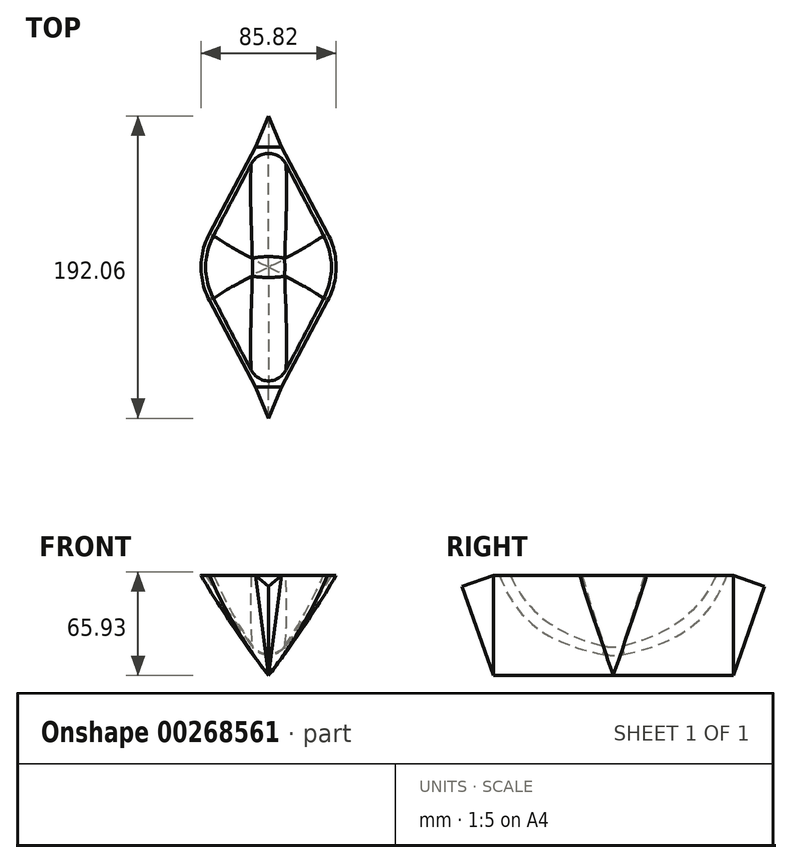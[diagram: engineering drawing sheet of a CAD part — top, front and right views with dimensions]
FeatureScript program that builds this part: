
annotation { "Feature Type Name" : "Feature", "Feature Type Description" : "" }
export const myFeature = defineFeature(function(context is Context, id is Id, definition is map)
    precondition{}
    {
        {
            var Q0;
            Q0=qCreatedBy(makeId("Front.planeOp"),FACE);
            var sketch = newSketch(context, id + "F0", { "sketchPlane" : qUnion([Q0])});
            skLineSegment(sketch, "E0", {"start": v(0, 0) * mm, "end": v(-48.84, 63.76) * mm});
            skLineSegment(sketch, "E1", {"start": v(-48.84, 63.76) * mm, "end": v(48.84, 63.76) * mm});
            skLineSegment(sketch, "E2", {"start": v(48.84, 63.76) * mm, "end": v(0, 0) * mm});
            skSolve(sketch);
        }
        {
            var Q0;
            Q0=qCreatedBy(makeId("Front.planeOp"),FACE);
            cPlane(context, id + "F1", {"entities" : qUnion([Q0]), "cplaneType" : CPlaneType.OFFSET, "offset" : 76.2 * mm, "width" : 152.4 * mm, "height" : 152.4 * mm});
        }
        {
            var Q0;
            Q0=qCreatedBy(id+"F1.planeOp",FACE);
            var sketch = newSketch(context, id + "F2", { "sketchPlane" : qUnion([Q0])});
            skLineSegment(sketch, "E3", {"start": v(0, 0) * mm, "end": v(-8.2, 63.76) * mm});
            skLineSegment(sketch, "E4", {"start": v(-8.2, 63.76) * mm, "end": v(8.2, 63.76) * mm});
            skLineSegment(sketch, "E5", {"start": v(8.2, 63.76) * mm, "end": v(0, 0) * mm});
            skSolve(sketch);
        }
        {
            var Q0;
            Q0=makeQuery(id+"F0.imprint","IMPRINT",FACE,{"disambiguationData":[TD([[makeQuery(id+"F0.imprint","IMPRINT",EDGE,{"derivedFrom":sQuery(id+"F0.wireOp",EDGE,"E0")}),-1.0]])]});
            var Q1;
            Q1=makeQuery(id+"F2.imprint","IMPRINT",FACE,{"disambiguationData":[TD([[makeQuery(id+"F2.imprint","IMPRINT",EDGE,{"derivedFrom":sQuery(id+"F2.wireOp",EDGE,"E3")}),-1.0]])]});
            loft(context, id + "F3", {"sheetProfilesArray" : [{ "sheetProfileEntities" : qUnion([Q0]) }, { "sheetProfileEntities" : qUnion([Q1]) }]});
        }
        {
            var Q0;
            Q0=makeQuery(id+"F3.opLoft","SWEPT_BODY",BODY,{"disambiguationData":[OSD([makeQuery(id+"F0.imprint","IMPRINT",FACE,{"disambiguationData":[TD([[makeQuery(id+"F0.imprint","IMPRINT",EDGE,{"derivedFrom":sQuery(id+"F0.wireOp",EDGE,"E0")}),-1.0]])]}),makeQuery(id+"F2.imprint","IMPRINT",FACE,{"disambiguationData":[TD([[makeQuery(id+"F2.imprint","IMPRINT",EDGE,{"derivedFrom":sQuery(id+"F2.wireOp",EDGE,"E3")}),-1.0]])]})])]});
            var Q1;
            Q1=qCreatedBy(makeId("Front.planeOp"),FACE);
            mirror(context, id + "F4", {"operationType" : NewBodyOperationType.ADD, "entities" : qUnion([Q0]), "mirrorPlane" : qUnion([Q1])});
        }
        {
            var Q0;
            {var subQ0=sQuery(id+"F0.wireOp",EDGE,"E2");var subQ1=sQuery(id+"F0.wireOp",EDGE,"E1");var subQ2=sQuery(id+"F0.wireOp",EDGE,"E0");var subQ3=makeQuery(id+"F3.opLoft","MID_CAP_EDGE",EDGE,{"disambiguationData":[OSD([subQ2,subQ1,subQ0]),TDD([makeQuery(id+"F0.imprint","INTERSECT",VERTEX,{"derivedFrom":[subQ2,subQ0]}),makeQuery(id+"F0.imprint","INTERSECT",VERTEX,{"derivedFrom":[subQ1,subQ0]}),makeQuery(id+"F0.imprint","IMPRINT",EDGE,{"derivedFrom":subQ0})])],"capPos":0.0});Q0=makeQuery(id+"F4.boolean.opBoolean","MERGE",EDGE,{"derivedFrom":[subQ3,makeQuery(id+"F4.opPattern","COPY",EDGE,{"derivedFrom":subQ3,"instanceName":"1"})]});}
            var Q1;
            {var subQ0=sQuery(id+"F0.wireOp",EDGE,"E0");var subQ1=sQuery(id+"F0.wireOp",EDGE,"E1");var subQ2=sQuery(id+"F0.wireOp",EDGE,"E2");var subQ3=makeQuery(id+"F3.opLoft","MID_CAP_EDGE",EDGE,{"disambiguationData":[OSD([subQ0,subQ1,subQ2]),TDD([makeQuery(id+"F0.imprint","INTERSECT",VERTEX,{"derivedFrom":[subQ0,subQ2]}),makeQuery(id+"F0.imprint","INTERSECT",VERTEX,{"derivedFrom":[subQ0,subQ1]}),makeQuery(id+"F0.imprint","IMPRINT",EDGE,{"derivedFrom":subQ0})])],"capPos":0.0});Q1=makeQuery(id+"F4.boolean.opBoolean","MERGE",EDGE,{"derivedFrom":[subQ3,makeQuery(id+"F4.opPattern","COPY",EDGE,{"derivedFrom":subQ3,"instanceName":"1"})]});}
            fillet(context, id + "F5", {"entities" : qUnion([Q0, Q1]), "radius" : 50.8 * mm, "tangentPropagation" : true, "allowEdgeOverflow" : false});
        }
        {
            var Q0;
            {var subQ0=sQuery(id+"F2.wireOp",EDGE,"E4");var subQ1=sQuery(id+"F2.wireOp",EDGE,"E5");var subQ2=sQuery(id+"F2.wireOp",EDGE,"E3");var subQ3=sQuery(id+"F0.wireOp",EDGE,"E1");var subQ4=sQuery(id+"F0.wireOp",EDGE,"E2");var subQ5=sQuery(id+"F0.wireOp",EDGE,"E0");var subQ6=makeQuery(id+"F3.opLoft","SWEPT_FACE",FACE,{"disambiguationData":[OSD([subQ5,subQ3,subQ4,subQ2,subQ0,subQ1]),TDD([makeQuery(id+"F0.imprint","INTERSECT",VERTEX,{"derivedFrom":[subQ5,subQ3]}),makeQuery(id+"F0.imprint","INTERSECT",VERTEX,{"derivedFrom":[subQ3,subQ4]}),makeQuery(id+"F0.imprint","IMPRINT",EDGE,{"derivedFrom":subQ3}),makeQuery(id+"F2.imprint","INTERSECT",VERTEX,{"derivedFrom":[subQ2,subQ0]}),makeQuery(id+"F2.imprint","INTERSECT",VERTEX,{"derivedFrom":[subQ0,subQ1]}),makeQuery(id+"F2.imprint","IMPRINT",EDGE,{"derivedFrom":subQ0})])]});Q0=makeQuery(id+"F4.boolean.opBoolean","MERGE",FACE,{"derivedFrom":[subQ6,makeQuery(id+"F4.opPattern","COPY",FACE,{"derivedFrom":subQ6,"instanceName":"1"})]});}
            shell(context, id + "F6", {"entities" : qUnion([Q0]), "thickness" : 2.54 * mm});
        }
        {
            var Q0;
            Q0=makeQuery(id+"F3.opLoft","CAP_FACE",FACE,{"disambiguationData":[OSD([makeQuery(id+"F2.imprint","IMPRINT",FACE,{"disambiguationData":[TD([[makeQuery(id+"F2.imprint","IMPRINT",EDGE,{"derivedFrom":sQuery(id+"F2.wireOp",EDGE,"E3")}),-1.0]])]})])],"isStart":true});
            extrude(context, id + "F7", {"entities" : qUnion([Q0]), "operationType" : NewBodyOperationType.ADD, "depth" : 25.4 * mm, "hasDraft" : true, "draftAngle" : 20 * degree, "draftPullDirection" : true});
        }
        {
            var Q0;
            Q0=makeQuery(id+"F3.opLoft","SWEPT_BODY",BODY,{"disambiguationData":[OSD([makeQuery(id+"F0.imprint","IMPRINT",FACE,{"disambiguationData":[TD([[makeQuery(id+"F0.imprint","IMPRINT",EDGE,{"derivedFrom":sQuery(id+"F0.wireOp",EDGE,"E0")}),-1.0]])]}),makeQuery(id+"F2.imprint","IMPRINT",FACE,{"disambiguationData":[TD([[makeQuery(id+"F2.imprint","IMPRINT",EDGE,{"derivedFrom":sQuery(id+"F2.wireOp",EDGE,"E3")}),-1.0]])]})])]});
            var Q1;
            Q1=qCreatedBy(makeId("Front.planeOp"),FACE);
            mirror(context, id + "F8", {"operationType" : NewBodyOperationType.ADD, "entities" : qUnion([Q0]), "mirrorPlane" : qUnion([Q1])});
        }
        {
            var Q0;
            {var subQ0=sQuery(id+"F2.wireOp",EDGE,"E5");var subQ1=sQuery(id+"F2.wireOp",EDGE,"E3");var subQ2=sQuery(id+"F0.wireOp",EDGE,"E2");var subQ3=sQuery(id+"F0.wireOp",EDGE,"E0");Q0=makeQuery(id+"F6.opShell","OFFSET_EDGE",EDGE,{"disambiguationData":[OSD([subQ3,subQ2,subQ1,subQ0]),TDD([makeQuery(id+"F4.opPattern","COPY",EDGE,{"derivedFrom":makeQuery(id+"F3.opLoft","SWEPT_EDGE",EDGE,{"disambiguationData":[OSD([subQ3,subQ2,subQ1,subQ0])]}),"instanceName":"1"})])]});}
            fillet(context, id + "F9", {"entities" : qUnion([Q0]), "radius" : 12.7 * mm, "tangentPropagation" : true, "allowEdgeOverflow" : false});
        }
    });
